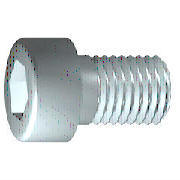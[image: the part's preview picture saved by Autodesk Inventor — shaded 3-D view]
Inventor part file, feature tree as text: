
AUTODESK INVENTOR PART (.ipt)
format: ipt  version: 2023.3 (Build 273359000, 359)  size: 191,488 bytes
history: native  units: mm (DEFAULTED — no unit token found)
features: sketch x2, other x1, extrude x1, plane x1, fillet x1
ambient origin geometry x7: Origin, YZ Plane, XY Plane, X Axis, Y Axis, Z Axis, Center Point
bodies: Solid1 (feature_tree)
feature tree (6):
  other  "Körper"
  extrude  "Loch"  Depth=3.0mm
  plane  "Work Plane1"
  fillet  "Fillet2"  Radius=3.0mm
  sketch  "Skizze1"  dims[d1=10.75mm d2=0.306825mm d3=3.0mm]
  sketch  "Skizze2"  dims[d4=1.3mm d5=60.0deg d6=3.0mm d7=3.0mm d8=2.886751mm d9=5.5mm d10=90.0deg d11=10.0mm d12=0.0mm d13=10.75mm d14=0.0mm d15=0.306725mm d16=0.306725mm d17=0.3mm d19=0.0mm d26=12.0mm d27=45.0deg d28=0.0mm d29=0.0mm d30=0.1mm]
